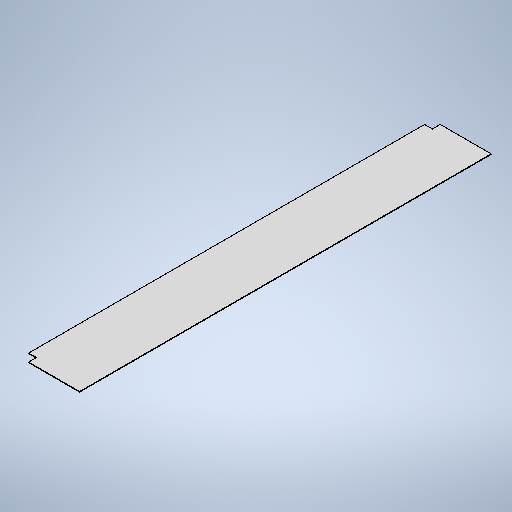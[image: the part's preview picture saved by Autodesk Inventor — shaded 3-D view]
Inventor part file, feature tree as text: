
AUTODESK INVENTOR PART (.ipt)
format: ipt  version: 2025.3 (Build 293356000, 356)  size: 304,128 bytes
history: native  units: mm
features: other x3, sketch x2, sheet_metal_op x1
ambient origin geometry x8: Origin, YZ Plane, XZ Plane, XY Plane, X Axis, Y Axis, Z Axis, Center Point
bodies: Solid1 (feature_tree)
feature tree (6):
  sheet_metal_op  "Face1"
  sketch  "Sketch1"  dims[d2=3.0mm]
  other  "Plate1"
  sketch  "Sketch5"  dims[d22=300.0mm d23=2100.0mm d24=40.0mm d25=40.0mm d28=90.0mm d29=90.0mm d31=100.0mm d32=2.0mm d33=5.0mm d34=4.0mm d35=0.5mm d36=5.0mm d37=5.0mm d38=5.0mm d39=2.0mm d40=3.0mm d41=0.0mm]
  other  "Cut1"
  other  "Definition1"
